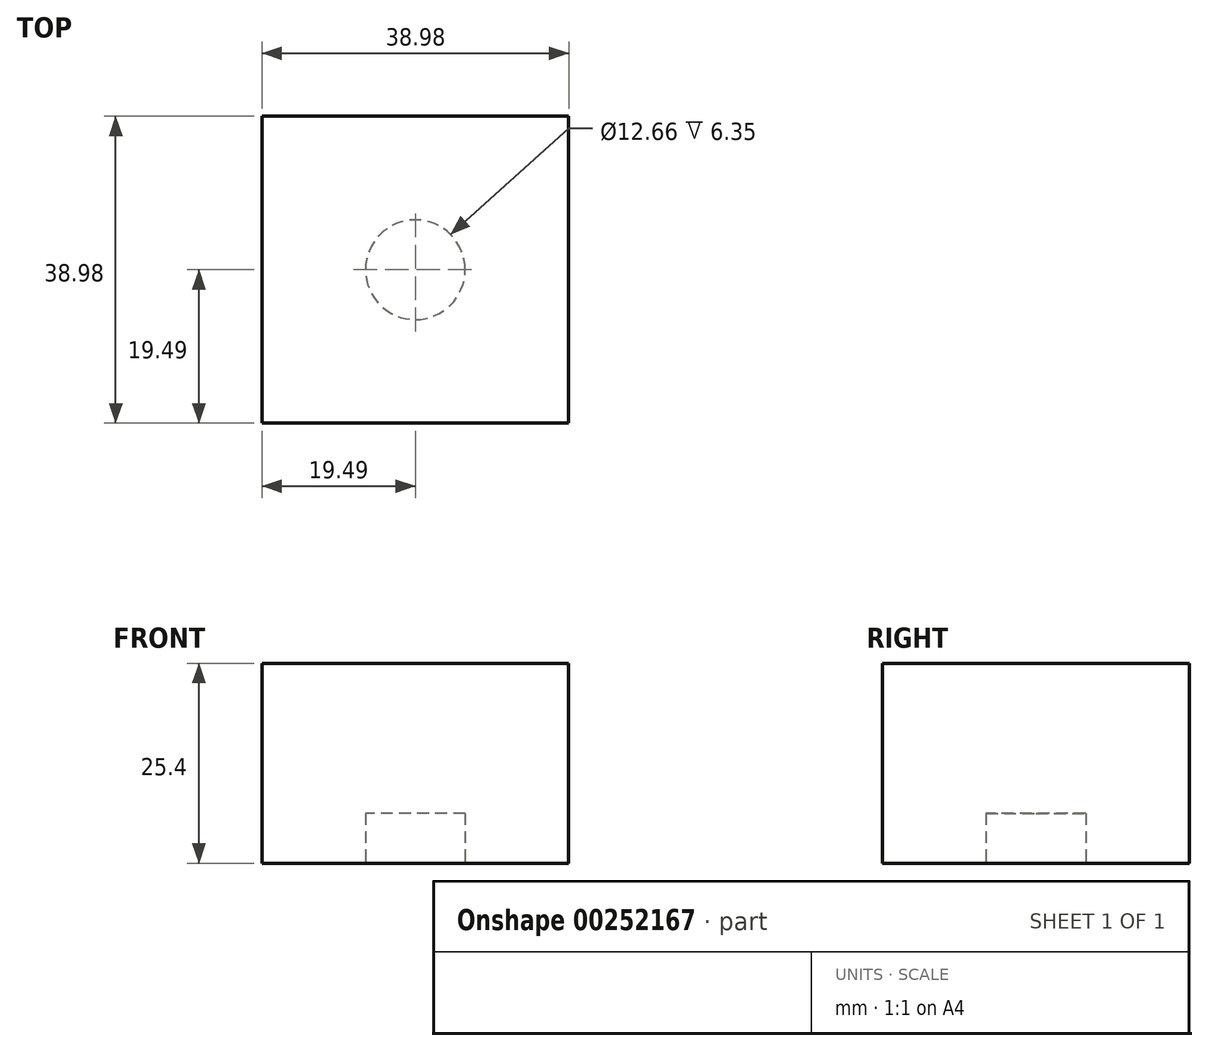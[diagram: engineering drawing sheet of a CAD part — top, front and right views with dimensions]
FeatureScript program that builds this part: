
annotation { "Feature Type Name" : "Feature", "Feature Type Description" : "" }
export const myFeature = defineFeature(function(context is Context, id is Id, definition is map)
    precondition{}
    {
        {
            var Q0;
            Q0=qCreatedBy(makeId("Top.planeOp"),FACE);
            var sketch = newSketch(context, id + "F0", { "sketchPlane" : qUnion([Q0])});
            skLineSegment(sketch, "E0.bottom", {"start": v(19.49, -19.49) * mm, "end": v(-19.49, -19.49) * mm});
            skLineSegment(sketch, "E0.top", {"start": v(19.49, 19.49) * mm, "end": v(-19.49, 19.49) * mm});
            skLineSegment(sketch, "E0.left", {"start": v(19.49, -19.49) * mm, "end": v(19.49, 19.49) * mm});
            skLineSegment(sketch, "E0.right", {"start": v(-19.49, -19.49) * mm, "end": v(-19.49, 19.49) * mm});
            skPoint(sketch, "E0.middle", {"position": v(0, 0) * mm});
            skSolve(sketch);
        }
        {
            var Q0;
            Q0 = qSketchRegion(id + "F0", true);
            extrude(context, id + "F1", {"entities" : qUnion([Q0]), "depth" : 25.4 * mm});
        }
        {
            var Q0;
            Q0=qCreatedBy(makeId("Top.planeOp"),FACE);
            var sketch = newSketch(context, id + "F2", { "sketchPlane" : qUnion([Q0])});
            skCircle(sketch, "E1", {"center": v(0, 0) * mm, "radius": 6.33 * mm});
            skSolve(sketch);
        }
        {
            var Q0;
            Q0 = qSketchRegion(id + "F2", true);
            extrude(context, id + "F3", {"entities" : qUnion([Q0]), "operationType" : NewBodyOperationType.REMOVE, "depth" : 6.35 * mm});
        }
    });
